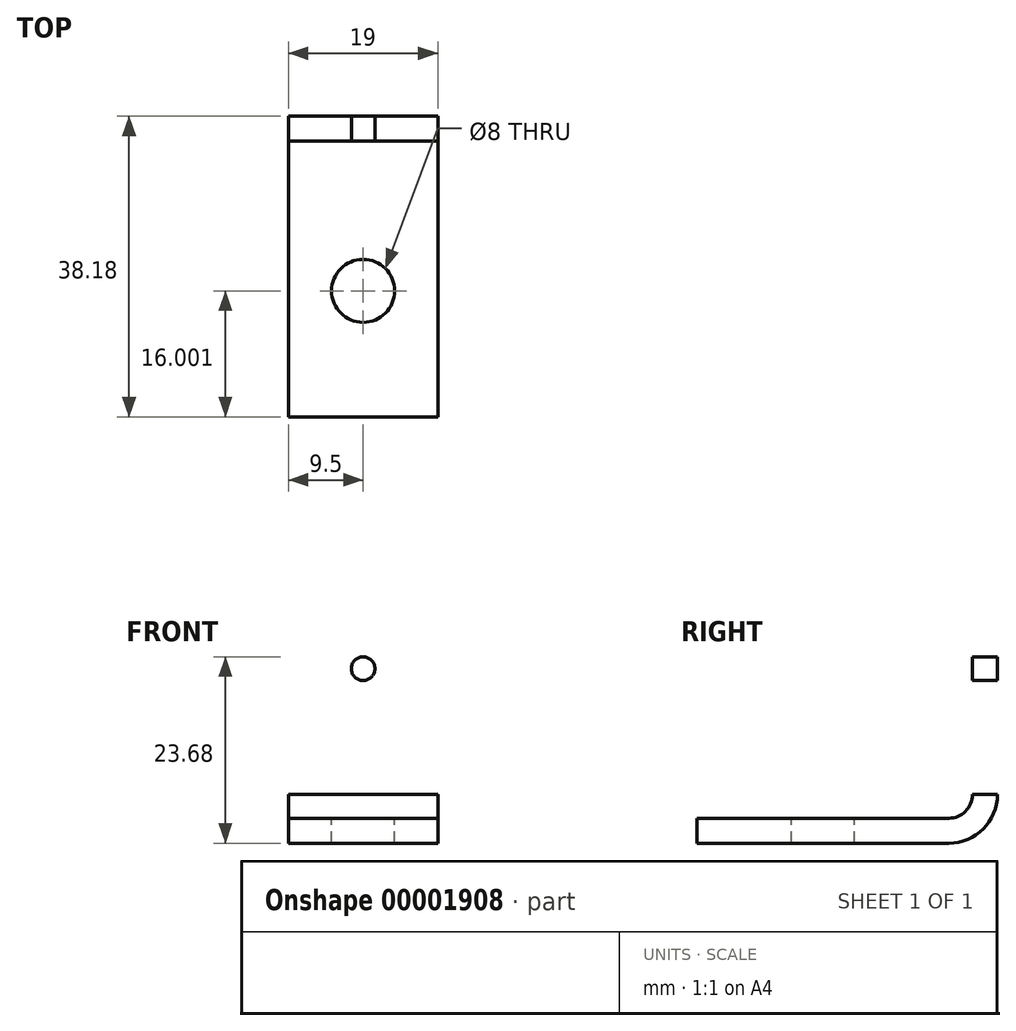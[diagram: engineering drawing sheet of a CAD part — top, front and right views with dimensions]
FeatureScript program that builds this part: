
annotation { "Feature Type Name" : "Feature", "Feature Type Description" : "" }
export const myFeature = defineFeature(function(context is Context, id is Id, definition is map)
    precondition{}
    {
        {
            var Q0;
            Q0=qCreatedBy(makeId("Right.planeOp"),FACE);
            var sketch = newSketch(context, id + "F0", { "sketchPlane" : qUnion([Q0])});
            skLineSegment(sketch, "E0", {"start": v(-0.9, 0) * mm, "end": v(31.1, 0) * mm});
            skLineSegment(sketch, "E1", {"start": v(34.1, 3) * mm, "end": v(34.1, 23) * mm});
            skPoint(sketch, "E2.visualSharp", {"position": v(34.1, 0) * mm});
            skArc(sketch, "E2.filletArc", {"start": v(31.1, 0) * mm, "mid": v(33.21, 0.88) * mm, "end": v(34.1, 3) * mm});
            skArc(sketch, "E3.0", {"start": v(31.1, -3.18) * mm, "mid": v(35.46, -1.37) * mm, "end": v(37.27, 3) * mm});
            skLineSegment(sketch, "E4.0", {"start": v(37.27, 3) * mm, "end": v(37.27, 23) * mm});
            skLineSegment(sketch, "E5.0", {"start": v(-0.9, -3.17) * mm, "end": v(31.1, -3.17) * mm});
            skLineSegment(sketch, "E6", {"start": v(-0.9, 0) * mm, "end": v(-0.9, -3.17) * mm});
            skLineSegment(sketch, "E7", {"start": v(34.1, 23) * mm, "end": v(37.27, 23) * mm});
            skSolve(sketch);
        }
        {
            var Q0;
            Q0=makeQuery(id+"F0.imprint","IMPRINT",FACE,{"disambiguationData":[TD([[makeQuery(id+"F0.imprint","IMPRINT",EDGE,{"derivedFrom":sQuery(id+"F0.wireOp",EDGE,"E0")}),-1.0]])]});
            extrude(context, id + "F1", {"entities" : qUnion([Q0]), "depth" : 19 * mm});
        }
        {
            var Q0;
            Q0=makeQuery(id+"F1.opExtrude","SWEPT_FACE",FACE,{"disambiguationData":[OSD([sQuery(id+"F0.wireOp",EDGE,"E4.0")])]});
            var sketch = newSketch(context, id + "F2", { "sketchPlane" : qUnion([Q0])});
            skLineSegment(sketch, "E8.0", {"start": v(-19, 23) * mm, "end": v(0, 23) * mm});
            skLineSegment(sketch, "E8.1", {"start": v(-19, 3) * mm, "end": v(-19, 23) * mm});
            skLineSegment(sketch, "E8.2", {"start": v(-19, 3) * mm, "end": v(0, 3) * mm});
            skLineSegment(sketch, "E8.3", {"start": v(0, 3) * mm, "end": v(0, 23) * mm});
            skLineSegment(sketch, "E9", {"start": v(-9.5, 23) * mm, "end": v(-9.5, 3) * mm});
            skCircle(sketch, "E10", {"center": v(-9.5, 19) * mm, "radius": 1.5 * mm});
            skCircle(sketch, "E11", {"center": v(-9.5, 7) * mm, "radius": 1.5 * mm});
            skLineSegment(sketch, "E12", {"start": v(-9.5, 13) * mm, "end": v(-13.84, 13) * mm});
            skCircle(sketch, "E13", {"center": v(-15.5, 13) * mm, "radius": 1.46 * mm});
            skPoint(sketch, "E13.centerSnap0", {"position": v(-11.67, 13) * mm});
            skCircle(sketch, "E14", {"center": v(-3.5, 13) * mm, "radius": 1.5 * mm});
            skSolve(sketch);
        }
        {
            var Q0;
            Q0=makeQuery(id+"F2.imprint","IMPRINT",FACE,{"disambiguationData":[TD([[makeQuery(id+"F2.imprint","IMPRINT",EDGE,{"derivedFrom":sQuery(id+"F2.wireOp",EDGE,"E14")}),1.0]])]});
            var Q1;
            Q1=makeQuery(id+"F2.imprint","IMPRINT",FACE,{"disambiguationData":[TD([[makeQuery(id+"F2.imprint","IMPRINT",EDGE,{"derivedFrom":sQuery(id+"F2.wireOp",EDGE,"E13")}),1.0]])]});
            var Q2;
            {var subQ0=sQuery(id+"F2.wireOp",EDGE,"E10");var subQ1=sQuery(id+"F2.wireOp",EDGE,"E9");var subQ2=makeQuery(id+"F2.imprint","INTERSECT",VERTEX,{"disambiguationData":[OD(0.0)],"derivedFrom":[subQ1,subQ0]});Q2=makeQuery(id+"F2.imprint","IMPRINT",FACE,{"disambiguationData":[TD([[makeQuery(id+"F2.imprint","IMPRINT",EDGE,{"disambiguationData":[TD([[subQ2,-1.0]])],"derivedFrom":subQ1}),-1.0]])]});}
            var Q3;
            {var subQ0=sQuery(id+"F2.wireOp",EDGE,"E10");var subQ1=sQuery(id+"F2.wireOp",EDGE,"E9");var subQ2=makeQuery(id+"F2.imprint","INTERSECT",VERTEX,{"disambiguationData":[OD(0.0)],"derivedFrom":[subQ1,subQ0]});Q3=makeQuery(id+"F2.imprint","IMPRINT",FACE,{"disambiguationData":[TD([[makeQuery(id+"F2.imprint","IMPRINT",EDGE,{"disambiguationData":[TD([[subQ2,-1.0]])],"derivedFrom":subQ1}),1.0]])]});}
            var Q4;
            {var subQ0=sQuery(id+"F2.wireOp",EDGE,"E11");var subQ1=sQuery(id+"F2.wireOp",EDGE,"E9");var subQ2=makeQuery(id+"F2.imprint","INTERSECT",VERTEX,{"disambiguationData":[OD(0.0)],"derivedFrom":[subQ1,subQ0]});Q4=makeQuery(id+"F2.imprint","IMPRINT",FACE,{"disambiguationData":[TD([[makeQuery(id+"F2.imprint","IMPRINT",EDGE,{"disambiguationData":[TD([[subQ2,-1.0]])],"derivedFrom":subQ1}),1.0]])]});}
            var Q5;
            {var subQ0=sQuery(id+"F2.wireOp",EDGE,"E11");var subQ1=sQuery(id+"F2.wireOp",EDGE,"E9");var subQ2=makeQuery(id+"F2.imprint","INTERSECT",VERTEX,{"disambiguationData":[OD(0.0)],"derivedFrom":[subQ1,subQ0]});Q5=makeQuery(id+"F2.imprint","IMPRINT",FACE,{"disambiguationData":[TD([[makeQuery(id+"F2.imprint","IMPRINT",EDGE,{"disambiguationData":[TD([[subQ2,-1.0]])],"derivedFrom":subQ1}),-1.0]])]});}
            var Q6;
            Q6=sQuery(id+"F2.wireOp",EDGE,"E10");
            var Q7;
            Q7=sQuery(id+"F2.wireOp",EDGE,"E14");
            var Q8;
            Q8=sQuery(id+"F2.wireOp",EDGE,"E11");
            var Q9;
            Q9=sQuery(id+"F2.wireOp",EDGE,"E13");
            extrude(context, id + "F3", {"entities" : qUnion([Q0, Q1, Q2, Q3, Q4, Q5]), "operationType" : NewBodyOperationType.REMOVE, "surfaceEntities" : qUnion([Q6, Q7, Q8, Q9]), "oppositeDirection" : true, "depth" : 6 * mm});
        }
        {
            var Q0;
            Q0=makeQuery(id+"F1.opExtrude","SWEPT_FACE",FACE,{"disambiguationData":[OSD([sQuery(id+"F0.wireOp",EDGE,"E0")])]});
            var sketch = newSketch(context, id + "F4", { "sketchPlane" : qUnion([Q0])});
            skCircle(sketch, "E15", {"center": v(9.5, 15.1) * mm, "radius": 4 * mm});
            skSolve(sketch);
        }
        {
            var Q0;
            Q0 = qSketchRegion(id + "F4", true);
            extrude(context, id + "F5", {"entities" : qUnion([Q0]), "operationType" : NewBodyOperationType.REMOVE, "oppositeDirection" : true, "depth" : 25 * mm});
        }
    });
